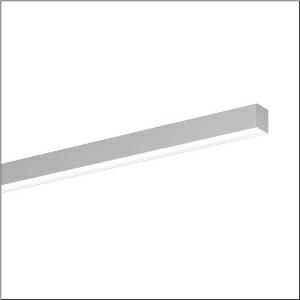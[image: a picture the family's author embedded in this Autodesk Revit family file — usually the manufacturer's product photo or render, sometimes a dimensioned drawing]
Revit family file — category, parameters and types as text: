
# Revit family: silica_r__21_51mx23tctas_d824
name_source: partatom
category: Lighting Fixtures
units: mm (PartAtom-declared; Revit-internal decimal feet)

## family parameters
Cut with Voids When Loaded = No
Host = Face
Light Source = No
Part Type = Normal
Room Calculation Point = No
Round Connector Dimension = Use Diameter
Shared = No

## types (1)
- --- (1 x LED, 8070 lm, 81.1 W, 6500K)
    Apparent Load = 81 VA
    CIE Flux Codes = 78 96 99 100 100
    Color Rendering = 80
    Color Temperature = 6500K
    Default Elevation = 1800 mm
    Description = Silica® 21, office luminaire, primary optical cover: prismatic diffuser, of PMMA, CAT 2 (L<= 3000cd/m²), light emission: direct distribution, primary light characteristic: symmetric, installation type: surface-mounted, LED, rated luminous flux: 8.070lm, luminous efficacy: 95lm/W, light colour: 8tw, colour temperature: 2700..6500K, control gear: DALI DT8, with terminal, 3+2-pole, max. 2.5mm², mains connection: 220..240V, AC, 50/60Hz, rated input power: 85.1W, luminaire housing, of aluminium, metallic grey (RAL 9006), length: 3.004mm, width: 53mm, height: 53mm, protection rating (complete): IP20, insulation class (complete): insulation class I (protective earthing), certification: CE, permissible operating ambient temperature: 0..+35°C, standard: EN 50419, packaging unit: 1 piece
    Height = 53 mm
    Lamp = 1 x LED
    Lamp Light Flux = 8070 lm
    Lamp Power = 81.1 W
    Lamp count = 1
    Length = 3004 mm
    Luminous efficacy = 100 lm/W
    Manufacturer = Siteco
    ModVariant = No
    Model = 51MX23TCTAS
    Mounting Place = Ceiling
    Mounting Type = Surface mounted
    Number of Poles = 1
    OnlyDefault = Yes
    Power Factor = 1
    Product Name = Silica® 21
    Product group = office luminaire | ceiling mounted
    ProductGroupID = 302
    Protection Class = Protection class I
    Protection Degree = IP 20
    RLX_Detail_Level = 1
    RLX_Emergency_Light_Flux = 0 lm
    RLX_Emergency_Type = 0
    RLX_Emergency_Type_DB = No
    RlxData = <blob elided: 17901 chars, md5=dfc1b08f>
    Socket = socket
    Standby Power = 0 W
    System Light Flux = 8070 lm
    System Power = 81 W
    Type Comments = individual setting
    Type Image = l_1335933.jpg
    URL = http://relux.com
    VarID = @adj_139788
    Voltage = 0 V
    Weight = 0.00 kg
    Width = 53 mm

## geometry (parser evidence)
native form markers: Blend x4, Sweep x10
no freeform markers — native parametric forms only
